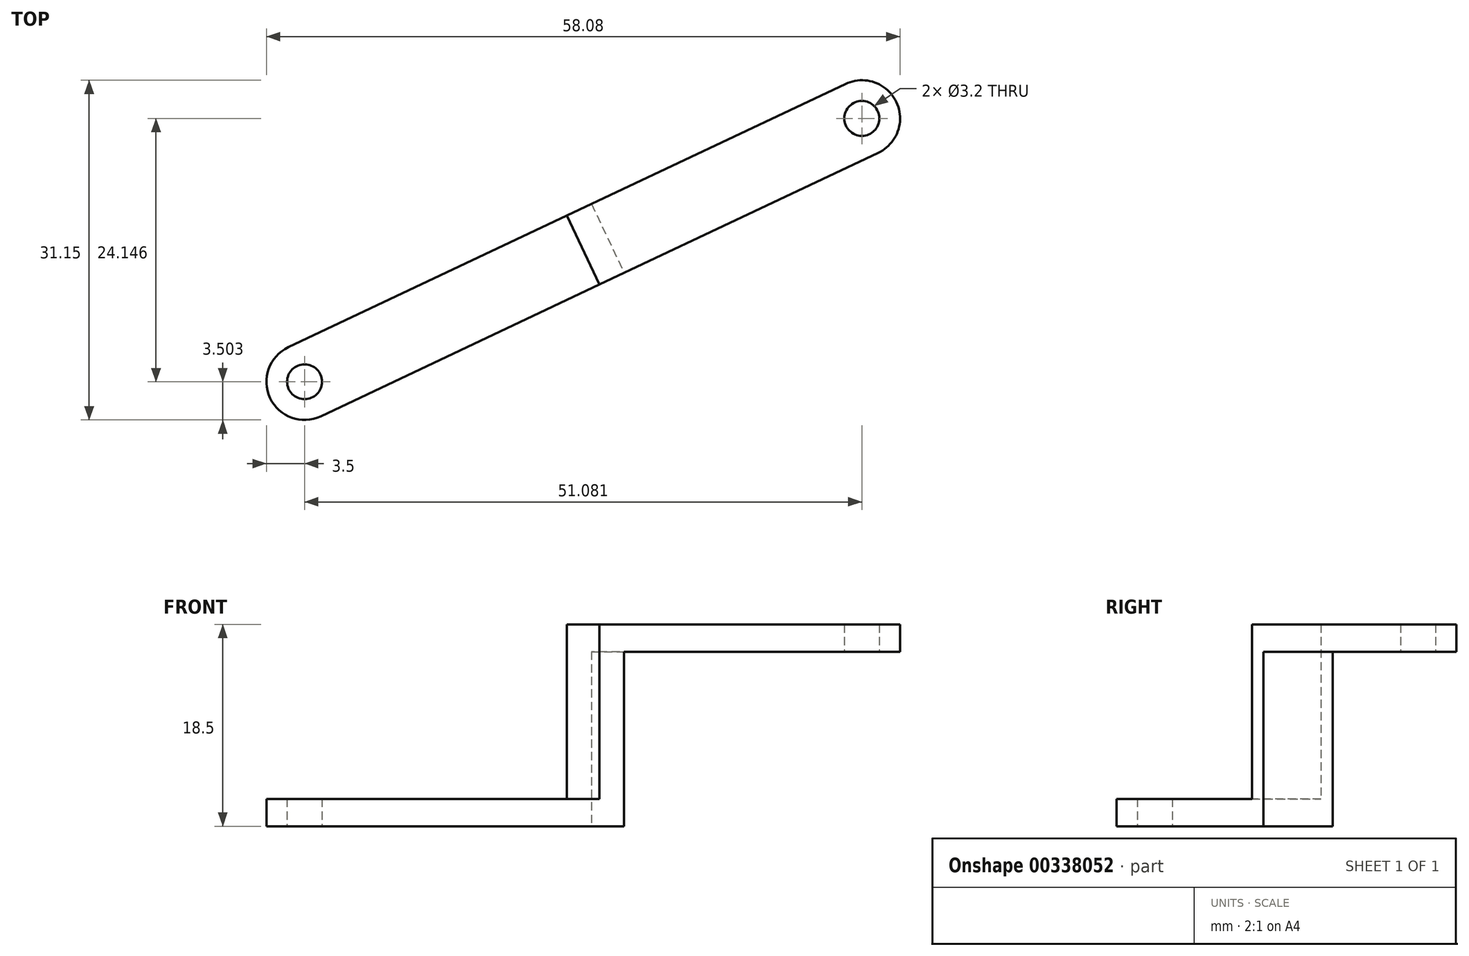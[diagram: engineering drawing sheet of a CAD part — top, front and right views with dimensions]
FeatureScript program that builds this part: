
annotation { "Feature Type Name" : "Feature", "Feature Type Description" : "" }
export const myFeature = defineFeature(function(context is Context, id is Id, definition is map)
    precondition{}
    {
        {
            var Q0;
            Q0=qCreatedBy(makeId("Top.planeOp"),FACE);
            cPlane(context, id + "F0", {"entities" : qUnion([Q0]), "cplaneType" : CPlaneType.OFFSET, "offset" : 16 * mm, "width" : 150 * mm, "height" : 150 * mm});
        }
        {
            var Q0;
            Q0=qCreatedBy(id+"F0.planeOp",FACE);
            var sketch = newSketch(context, id + "F1", { "sketchPlane" : qUnion([Q0])});
            skLineSegment(sketch, "E0", {"start": v(0, 0) * mm, "end": v(46.56, 22) * mm, "construction": true});
            skCircle(sketch, "E1", {"center": v(46.56, 22) * mm, "radius": 1.6 * mm});
            skCircle(sketch, "E2", {"center": v(46.56, 22) * mm, "radius": 3.5 * mm});
            skLineSegment(sketch, "E3", {"start": v(45.06, 25.17) * mm, "end": v(21.78, 14.17) * mm});
            skLineSegment(sketch, "E4.MirrorCS", {"start": v(48.06, 18.84) * mm, "end": v(24.78, 7.84) * mm});
            skLineSegment(sketch, "E5", {"start": v(21.78, 14.17) * mm, "end": v(24.78, 7.84) * mm});
            skSolve(sketch);
        }
        {
            var Q0;
            Q0=qSketchRegion(id+"F1",true);
            extrude(context, id + "F2", {"entities" : qUnion([Q0]), "depth" : 2.5 * mm});
        }
        {
            var Q0;
            Q0=makeQuery(id+"F2.opExtrude","SWEPT_FACE",FACE,{"disambiguationData":[OSD([sQuery(id+"F1.wireOp",EDGE,"E5")])]});
            var sketch = newSketch(context, id + "F3", { "sketchPlane" : qUnion([Q0])});
            skLineSegment(sketch, "E6.bottom", {"start": v(-3.5, 18.5) * mm, "end": v(3.5, 18.5) * mm});
            skLineSegment(sketch, "E6.top", {"start": v(-3.5, 0) * mm, "end": v(3.5, 0) * mm});
            skLineSegment(sketch, "E6.left", {"start": v(-3.5, 18.5) * mm, "end": v(-3.5, 0) * mm});
            skLineSegment(sketch, "E6.right", {"start": v(3.5, 18.5) * mm, "end": v(3.5, 0) * mm});
            skSolve(sketch);
        }
        {
            var Q0;
            Q0=qSketchRegion(id+"F3",true);
            extrude(context, id + "F4", {"entities" : qUnion([Q0]), "operationType" : NewBodyOperationType.ADD, "depth" : 2.5 * mm});
        }
        {
            var Q0;
            Q0=qCreatedBy(makeId("Top.planeOp"),FACE);
            var sketch = newSketch(context, id + "F5", { "sketchPlane" : qUnion([Q0])});
            skCircle(sketch, "E7", {"center": v(-4.52, -2.14) * mm, "radius": 1.6 * mm});
            skCircle(sketch, "E8", {"center": v(-4.52, -2.14) * mm, "radius": 3.5 * mm});
            skLineSegment(sketch, "E9", {"start": v(-4.52, -2.14) * mm, "end": v(18.3, 8.65) * mm, "construction": true});
            skLineSegment(sketch, "E10", {"start": v(-6.02, 1.03) * mm, "end": v(19.52, 13.1) * mm});
            skLineSegment(sketch, "E11.MirrorCS", {"start": v(-3.02, -5.3) * mm, "end": v(22.52, 6.77) * mm});
            skLineSegment(sketch, "E12.0", {"start": v(19.52, 13.1) * mm, "end": v(22.52, 6.77) * mm});
            skCircle(sketch, "E13", {"center": v(-4.52, -2.14) * mm, "radius": 1.5 * mm, "construction": true});
            skSolve(sketch);
        }
        {
            var Q0;
            Q0=qSketchRegion(id+"F5",true);
            extrude(context, id + "F6", {"entities" : qUnion([Q0]), "operationType" : NewBodyOperationType.ADD, "depth" : 2.5 * mm});
        }
    });
